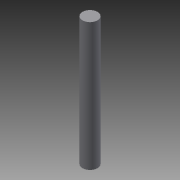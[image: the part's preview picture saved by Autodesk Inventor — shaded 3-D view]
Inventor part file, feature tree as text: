
AUTODESK INVENTOR PART (.ipt)
format: ipt  version: 2015 (Build 190159000, 159)  size: 79,872 bytes
history: native  units: in
note: dims shown in document units (in); Inventor stores cm internally (conversion verified against a paired STEP export)
features: extrude x1, sketch x1
ambient origin geometry x8: Origin, YZ Plane, XZ Plane, XY Plane, X Axis, Y Axis, Z Axis, Center Point
bodies: Solid1 (feature_tree)
feature tree (2):
  extrude  "Extrusion1"  Depth=23.622in TaperAngle=0.0deg
  sketch  "Sketch1"  dims[d0=2.7559in d1=23.622in d2=0.0in]
